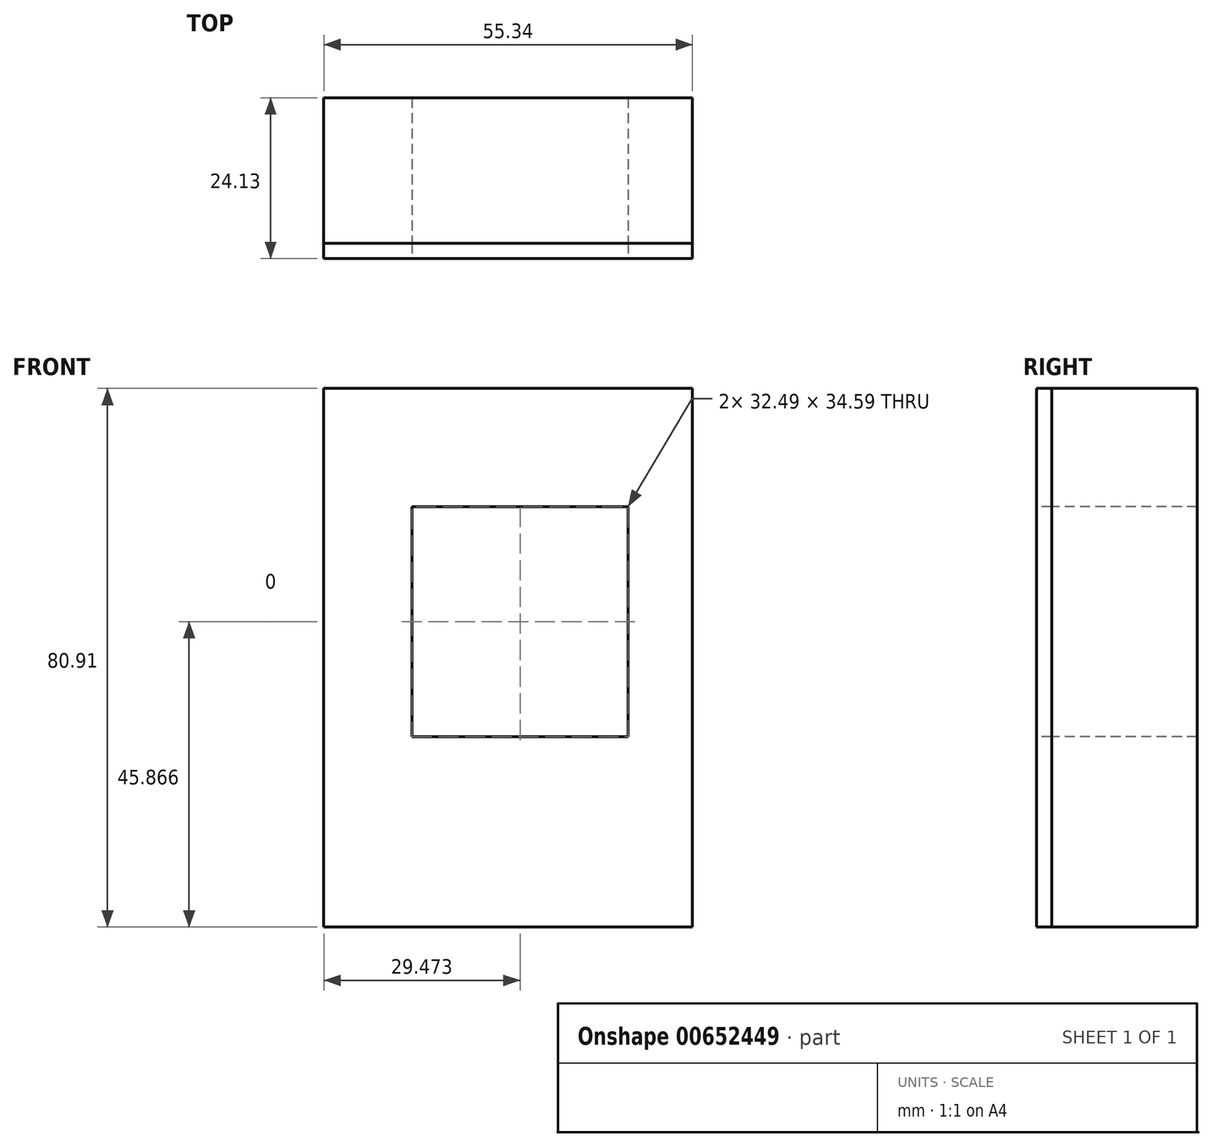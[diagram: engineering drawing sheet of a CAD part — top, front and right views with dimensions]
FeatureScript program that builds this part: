
annotation { "Feature Type Name" : "Feature", "Feature Type Description" : "" }
export const myFeature = defineFeature(function(context is Context, id is Id, definition is map)
    precondition{}
    {
        {
            var Q0;
            Q0=qCreatedBy(makeId("Front.planeOp"),FACE);
            var sketch = newSketch(context, id + "F0", { "sketchPlane" : qUnion([Q0])});
            skLineSegment(sketch, "E0.bottom", {"start": v(-28.42, 37.45) * mm, "end": v(26.92, 37.45) * mm});
            skLineSegment(sketch, "E0.top", {"start": v(-28.42, -43.46) * mm, "end": v(26.92, -43.46) * mm});
            skLineSegment(sketch, "E0.left", {"start": v(-28.42, 37.45) * mm, "end": v(-28.42, -43.46) * mm});
            skLineSegment(sketch, "E0.right", {"start": v(26.92, 37.45) * mm, "end": v(26.92, -43.46) * mm});
            skSolve(sketch);
        }
        {
            var Q0;
            Q0 = qSketchRegion(id + "F0", true);
            extrude(context, id + "F1", {"entities" : qUnion([Q0]), "depth" : 21.84 * mm, "offsetDistance" : 25.4 * mm});
        }
        {
            var Q0;
            Q0=makeQuery(id+"F1.opExtrude","CAP_FACE",FACE,{"disambiguationData":[OSD([sQuery(id+"F0.wireOp",EDGE,"E0.bottom"),sQuery(id+"F0.wireOp",EDGE,"E0.top"),sQuery(id+"F0.wireOp",EDGE,"E0.left"),sQuery(id+"F0.wireOp",EDGE,"E0.right")])],"isStart":false});
            var sketch = newSketch(context, id + "F2", { "sketchPlane" : qUnion([Q0])});
            skLineSegment(sketch, "E1", {"start": v(-9.78, 11.88) * mm, "end": v(10.08, 11.88) * mm});
            skLineSegment(sketch, "E2", {"start": v(10.08, 11.88) * mm, "end": v(10.08, 0) * mm});
            skLineSegment(sketch, "E3", {"start": v(10.08, 0) * mm, "end": v(4.96, 0) * mm});
            skLineSegment(sketch, "E4", {"start": v(4.96, 0) * mm, "end": v(4.96, -6.77) * mm});
            skLineSegment(sketch, "E5", {"start": v(4.96, -6.77) * mm, "end": v(-3.46, -6.77) * mm});
            skLineSegment(sketch, "E6", {"start": v(-3.46, -6.77) * mm, "end": v(-3.46, 0) * mm});
            skLineSegment(sketch, "E7", {"start": v(-3.46, 0) * mm, "end": v(-9.78, 0) * mm});
            skLineSegment(sketch, "E8", {"start": v(-9.78, 0) * mm, "end": v(-9.78, 11.88) * mm});
            skSolve(sketch);
        }
        {
            var Q0;
            Q0 = qSketchRegion(id + "F2", true);
            extrude(context, id + "F3", {"entities" : qUnion([Q0]), "operationType" : NewBodyOperationType.REMOVE, "oppositeDirection" : true, "depth" : 12.7 * mm, "offsetDistance" : 25.4 * mm});
        }
        {
            var Q0;
            Q0=makeQuery(id+"F1.opExtrude","CAP_FACE",FACE,{"disambiguationData":[OSD([sQuery(id+"F0.wireOp",EDGE,"E0.bottom"),sQuery(id+"F0.wireOp",EDGE,"E0.top"),sQuery(id+"F0.wireOp",EDGE,"E0.left"),sQuery(id+"F0.wireOp",EDGE,"E0.right")])],"isStart":false});
            var sketch = newSketch(context, id + "F4", { "sketchPlane" : qUnion([Q0])});
            skLineSegment(sketch, "E9.bottom", {"start": v(-28.42, 37.45) * mm, "end": v(26.92, 37.45) * mm});
            skLineSegment(sketch, "E9.top", {"start": v(-28.42, -43.46) * mm, "end": v(26.92, -43.46) * mm});
            skLineSegment(sketch, "E9.left", {"start": v(-28.42, 37.45) * mm, "end": v(-28.42, -43.46) * mm});
            skLineSegment(sketch, "E9.right", {"start": v(26.92, 37.45) * mm, "end": v(26.92, -43.46) * mm});
            skSolve(sketch);
        }
        {
            var Q0;
            Q0 = qSketchRegion(id + "F4", true);
            extrude(context, id + "F5", {"entities" : qUnion([Q0]), "depth" : 2.3 * mm, "offsetDistance" : 25.4 * mm});
        }
        {
            var Q0;
            Q0=makeQuery(id+"F5.opExtrude","CAP_FACE",FACE,{"disambiguationData":[OSD([sQuery(id+"F4.wireOp",EDGE,"E9.bottom"),sQuery(id+"F4.wireOp",EDGE,"E9.top"),sQuery(id+"F4.wireOp",EDGE,"E9.left"),sQuery(id+"F4.wireOp",EDGE,"E9.right")])],"isStart":false});
            var sketch = newSketch(context, id + "F6", { "sketchPlane" : qUnion([Q0])});
            skLineSegment(sketch, "E10.bottom", {"start": v(-15.19, 19.7) * mm, "end": v(17.3, 19.7) * mm});
            skLineSegment(sketch, "E10.top", {"start": v(-15.19, -14.89) * mm, "end": v(17.3, -14.89) * mm});
            skLineSegment(sketch, "E10.left", {"start": v(-15.19, 19.7) * mm, "end": v(-15.19, -14.89) * mm});
            skLineSegment(sketch, "E10.right", {"start": v(17.3, 19.7) * mm, "end": v(17.3, -14.89) * mm});
            skSolve(sketch);
        }
        {
            var Q0;
            Q0 = qSketchRegion(id + "F6", true);
            extrude(context, id + "F7", {"entities" : qUnion([Q0]), "operationType" : NewBodyOperationType.REMOVE, "oppositeDirection" : true, "depth" : 25.4 * mm, "offsetDistance" : 25.4 * mm});
        }
    });
